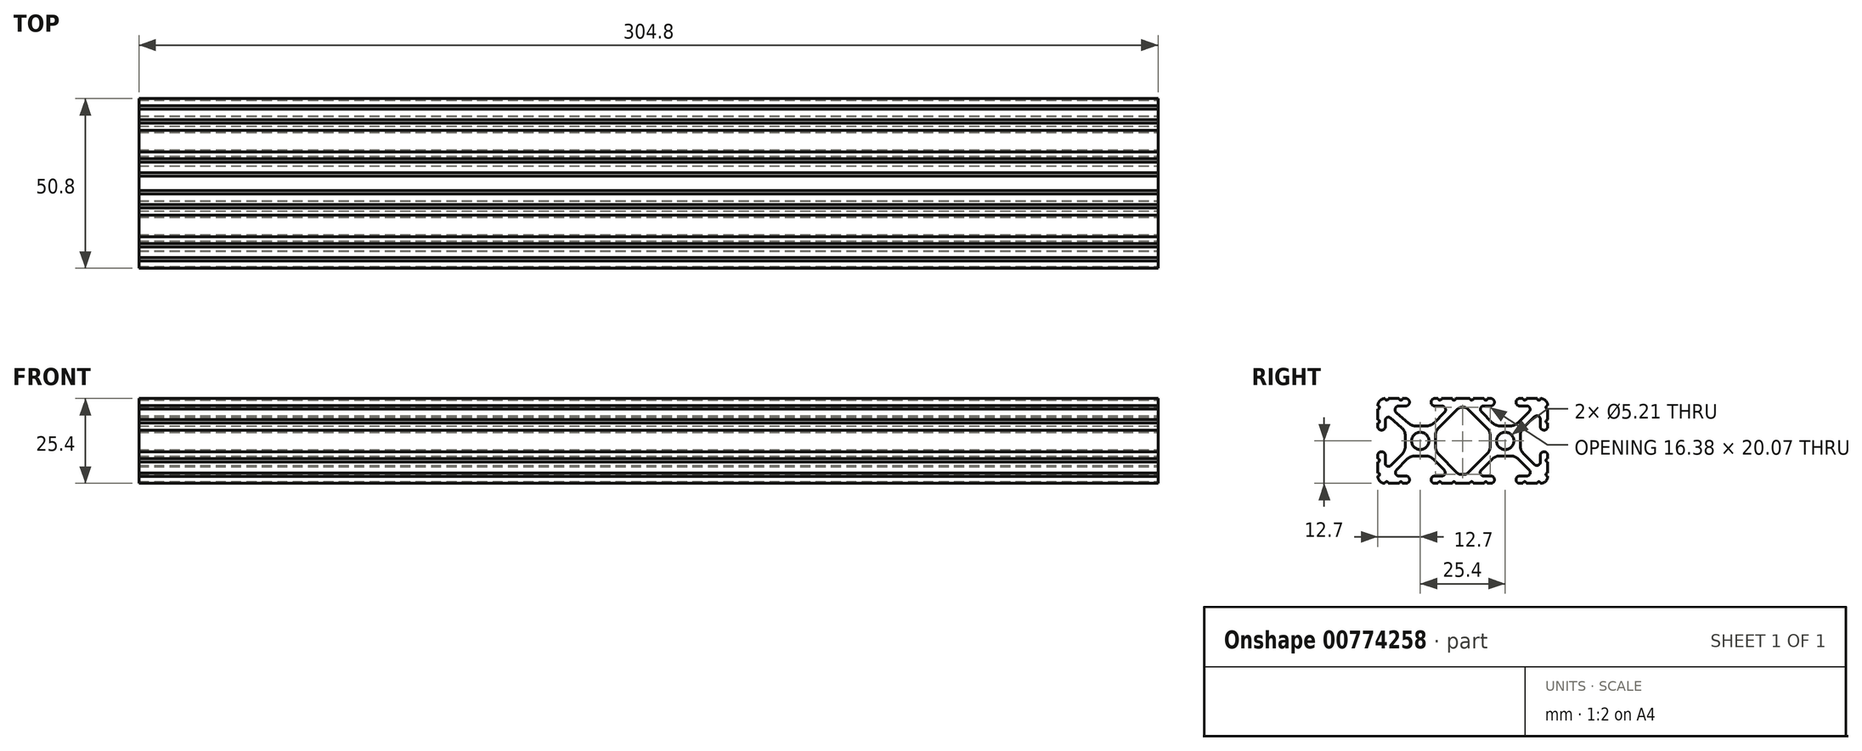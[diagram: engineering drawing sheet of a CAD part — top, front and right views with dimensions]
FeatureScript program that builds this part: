
annotation { "Feature Type Name" : "Feature", "Feature Type Description" : "" }
export const myFeature = defineFeature(function(context is Context, id is Id, definition is map)
    precondition{}
    {
        {
            var Q0;
            Q0=qCreatedBy(makeId("Right.planeOp"),FACE);
            var sketch = newSketch(context, id + "F0", { "sketchPlane" : qUnion([Q0])});
            skLineSegment(sketch, "E0", {"start": v(7.26, 3.87) * mm, "end": v(1.55, 9.57) * mm});
            skArc(sketch, "E1", {"start": v(1.55, 9.57) * mm, "mid": v(1.04, 9.91) * mm, "end": v(0.43, 10.03) * mm});
            skLineSegment(sketch, "E2", {"start": v(0.43, 10.03) * mm, "end": v(-0.43, 10.03) * mm});
            skArc(sketch, "E3", {"start": v(-0.43, 10.03) * mm, "mid": v(-1.04, 9.91) * mm, "end": v(-1.55, 9.57) * mm});
            skLineSegment(sketch, "E4", {"start": v(-1.55, 9.57) * mm, "end": v(-7.26, 3.87) * mm});
            skArc(sketch, "E5", {"start": v(-7.26, 3.87) * mm, "mid": v(-7.95, 2.84) * mm, "end": v(-8.2, 1.62) * mm});
            skLineSegment(sketch, "E6", {"start": v(-8.2, 1.62) * mm, "end": v(-8.2, -1.62) * mm});
            skLineSegment(sketch, "E7", {"start": v(-7.28, -3.85) * mm, "end": v(-1.68, -9.56) * mm});
            skArc(sketch, "E8", {"start": v(-1.68, -9.56) * mm, "mid": v(-1.16, -9.91) * mm, "end": v(-0.55, -10.03) * mm});
            skLineSegment(sketch, "E9", {"start": v(-0.55, -10.03) * mm, "end": v(0.4, -10.03) * mm});
            skArc(sketch, "E10", {"start": v(0.4, -10.03) * mm, "mid": v(1, -9.91) * mm, "end": v(1.5, -9.58) * mm});
            skLineSegment(sketch, "E11", {"start": v(1.5, -9.58) * mm, "end": v(7.25, -3.88) * mm});
            skArc(sketch, "E12", {"start": v(7.25, -3.88) * mm, "mid": v(7.95, -2.84) * mm, "end": v(8.2, -1.62) * mm});
            skLineSegment(sketch, "E13", {"start": v(8.2, -1.62) * mm, "end": v(8.2, 1.62) * mm});
            skArc(sketch, "E14", {"start": v(8.2, 1.62) * mm, "mid": v(7.95, 2.84) * mm, "end": v(7.26, 3.87) * mm});
            skCircle(sketch, "E15", {"center": v(12.7, 0) * mm, "radius": 2.6 * mm});
            skCircle(sketch, "E16", {"center": v(-12.7, 0) * mm, "radius": 2.6 * mm});
            skArc(sketch, "E17", {"start": v(-8.2, -1.62) * mm, "mid": v(-7.96, -2.82) * mm, "end": v(-7.28, -3.85) * mm});
            skLineSegment(sketch, "E18", {"start": v(-15.94, -11.65) * mm, "end": v(-15.94, -11.54) * mm});
            skArc(sketch, "E19", {"start": v(-15.94, -11.54) * mm, "mid": v(-16.25, -10.8) * mm, "end": v(-16.99, -10.5) * mm});
            skLineSegment(sketch, "E20", {"start": v(-16.99, -10.5) * mm, "end": v(-19.12, -10.5) * mm});
            skArc(sketch, "E21", {"start": v(-19.84, -8.77) * mm, "mid": v(-20.05, -9.87) * mm, "end": v(-19.12, -10.5) * mm});
            skLineSegment(sketch, "E22", {"start": v(-19.84, -8.77) * mm, "end": v(-16.62, -5.46) * mm});
            skArc(sketch, "E23", {"start": v(-14.34, -4.5) * mm, "mid": v(-15.58, -4.75) * mm, "end": v(-16.62, -5.46) * mm});
            skLineSegment(sketch, "E24", {"start": v(-14.34, -4.5) * mm, "end": v(-11.08, -4.5) * mm});
            skArc(sketch, "E25", {"start": v(-8.82, -5.45) * mm, "mid": v(-9.85, -4.74) * mm, "end": v(-11.08, -4.5) * mm});
            skLineSegment(sketch, "E26", {"start": v(-8.82, -5.45) * mm, "end": v(-5.56, -8.76) * mm});
            skArc(sketch, "E27", {"start": v(-6.29, -10.5) * mm, "mid": v(-5.35, -9.87) * mm, "end": v(-5.56, -8.76) * mm});
            skLineSegment(sketch, "E28", {"start": v(-6.29, -10.5) * mm, "end": v(-8.41, -10.5) * mm});
            skArc(sketch, "E29", {"start": v(-8.41, -10.5) * mm, "mid": v(-9.15, -10.8) * mm, "end": v(-9.46, -11.54) * mm});
            skLineSegment(sketch, "E30", {"start": v(-9.46, -11.54) * mm, "end": v(-9.46, -11.65) * mm});
            skArc(sketch, "E31", {"start": v(-9.46, -11.65) * mm, "mid": v(-9.15, -12.4) * mm, "end": v(-8.41, -12.7) * mm});
            skLineSegment(sketch, "E32", {"start": v(-8.41, -12.7) * mm, "end": v(-7.38, -12.7) * mm});
            skArc(sketch, "E33", {"start": v(-6.37, -12.7) * mm, "mid": v(-6.87, -12.2) * mm, "end": v(-7.38, -12.7) * mm});
            skLineSegment(sketch, "E34", {"start": v(-6.37, -12.7) * mm, "end": v(-3.15, -12.7) * mm});
            skArc(sketch, "E35", {"start": v(-2.13, -12.7) * mm, "mid": v(-2.64, -12.2) * mm, "end": v(-3.15, -12.7) * mm});
            skLineSegment(sketch, "E36", {"start": v(-2.13, -12.7) * mm, "end": v(2.13, -12.7) * mm});
            skArc(sketch, "E37", {"start": v(3.15, -12.7) * mm, "mid": v(2.64, -12.2) * mm, "end": v(2.13, -12.7) * mm});
            skLineSegment(sketch, "E38", {"start": v(3.15, -12.7) * mm, "end": v(6.37, -12.7) * mm});
            skArc(sketch, "E39", {"start": v(7.38, -12.7) * mm, "mid": v(6.87, -12.2) * mm, "end": v(6.37, -12.7) * mm});
            skLineSegment(sketch, "E40", {"start": v(7.38, -12.7) * mm, "end": v(8.41, -12.7) * mm});
            skArc(sketch, "E41", {"start": v(8.41, -12.7) * mm, "mid": v(9.15, -12.4) * mm, "end": v(9.46, -11.65) * mm});
            skLineSegment(sketch, "E42", {"start": v(9.46, -11.65) * mm, "end": v(9.46, -11.54) * mm});
            skArc(sketch, "E43", {"start": v(9.46, -11.54) * mm, "mid": v(9.15, -10.8) * mm, "end": v(8.41, -10.5) * mm});
            skLineSegment(sketch, "E44", {"start": v(8.41, -10.5) * mm, "end": v(6.28, -10.5) * mm});
            skArc(sketch, "E45", {"start": v(5.53, -8.67) * mm, "mid": v(5.3, -9.83) * mm, "end": v(6.28, -10.5) * mm});
            skLineSegment(sketch, "E46", {"start": v(5.53, -8.67) * mm, "end": v(8.8, -5.42) * mm});
            skArc(sketch, "E47", {"start": v(11.05, -4.5) * mm, "mid": v(9.84, -4.73) * mm, "end": v(8.8, -5.42) * mm});
            skLineSegment(sketch, "E48", {"start": v(11.05, -4.5) * mm, "end": v(14.35, -4.5) * mm});
            skArc(sketch, "E49", {"start": v(16.6, -5.42) * mm, "mid": v(15.56, -4.73) * mm, "end": v(14.35, -4.5) * mm});
            skLineSegment(sketch, "E50", {"start": v(16.6, -5.42) * mm, "end": v(19.87, -8.67) * mm});
            skArc(sketch, "E51", {"start": v(19.12, -10.5) * mm, "mid": v(20.1, -9.83) * mm, "end": v(19.87, -8.67) * mm});
            skLineSegment(sketch, "E52", {"start": v(19.12, -10.5) * mm, "end": v(16.99, -10.5) * mm});
            skArc(sketch, "E53", {"start": v(16.99, -10.5) * mm, "mid": v(16.25, -10.8) * mm, "end": v(15.94, -11.54) * mm});
            skLineSegment(sketch, "E54", {"start": v(15.94, -11.54) * mm, "end": v(15.94, -11.65) * mm});
            skArc(sketch, "E55", {"start": v(15.94, -11.65) * mm, "mid": v(16.25, -12.4) * mm, "end": v(16.99, -12.7) * mm});
            skLineSegment(sketch, "E56", {"start": v(16.99, -12.7) * mm, "end": v(18.02, -12.7) * mm});
            skArc(sketch, "E57", {"start": v(19.03, -12.7) * mm, "mid": v(18.53, -12.2) * mm, "end": v(18.02, -12.7) * mm});
            skLineSegment(sketch, "E58", {"start": v(19.03, -12.7) * mm, "end": v(22.25, -12.7) * mm});
            skArc(sketch, "E59", {"start": v(23.27, -12.7) * mm, "mid": v(22.76, -12.2) * mm, "end": v(22.25, -12.7) * mm});
            skArc(sketch, "E60", {"start": v(23.27, -12.7) * mm, "mid": v(24.78, -12.08) * mm, "end": v(25.4, -10.57) * mm});
            skArc(sketch, "E61", {"start": v(25.4, -9.55) * mm, "mid": v(24.9, -10.06) * mm, "end": v(25.4, -10.57) * mm});
            skLineSegment(sketch, "E62", {"start": v(25.4, -9.55) * mm, "end": v(25.4, -6.33) * mm});
            skArc(sketch, "E63", {"start": v(25.4, -5.32) * mm, "mid": v(24.9, -5.83) * mm, "end": v(25.4, -6.33) * mm});
            skLineSegment(sketch, "E64", {"start": v(25.4, -5.32) * mm, "end": v(25.4, -4.24) * mm});
            skArc(sketch, "E65", {"start": v(25.4, -4.24) * mm, "mid": v(25.1, -3.53) * mm, "end": v(24.4, -3.24) * mm});
            skLineSegment(sketch, "E66", {"start": v(24.4, -3.24) * mm, "end": v(24.24, -3.24) * mm});
            skArc(sketch, "E67", {"start": v(24.24, -3.24) * mm, "mid": v(23.5, -3.55) * mm, "end": v(23.2, -4.29) * mm});
            skLineSegment(sketch, "E68", {"start": v(23.2, -4.29) * mm, "end": v(23.2, -6.33) * mm});
            skArc(sketch, "E69", {"start": v(21.43, -7.07) * mm, "mid": v(22.56, -7.29) * mm, "end": v(23.2, -6.33) * mm});
            skLineSegment(sketch, "E70", {"start": v(21.43, -7.07) * mm, "end": v(18.15, -3.8) * mm});
            skArc(sketch, "E71", {"start": v(17.2, -1.55) * mm, "mid": v(17.45, -2.77) * mm, "end": v(18.15, -3.8) * mm});
            skLineSegment(sketch, "E72", {"start": v(17.2, -1.55) * mm, "end": v(17.2, 1.7) * mm});
            skArc(sketch, "E73", {"start": v(18.14, 3.94) * mm, "mid": v(17.45, 2.91) * mm, "end": v(17.2, 1.7) * mm});
            skLineSegment(sketch, "E74", {"start": v(18.14, 3.94) * mm, "end": v(21.43, 7.23) * mm});
            skArc(sketch, "E75", {"start": v(23.2, 6.5) * mm, "mid": v(22.55, 7.45) * mm, "end": v(21.43, 7.23) * mm});
            skLineSegment(sketch, "E76", {"start": v(23.2, 6.5) * mm, "end": v(23.2, 4.29) * mm});
            skArc(sketch, "E77", {"start": v(23.2, 4.29) * mm, "mid": v(23.5, 3.55) * mm, "end": v(24.24, 3.24) * mm});
            skLineSegment(sketch, "E78", {"start": v(24.24, 3.24) * mm, "end": v(24.35, 3.24) * mm});
            skArc(sketch, "E79", {"start": v(24.35, 3.24) * mm, "mid": v(25.1, 3.55) * mm, "end": v(25.4, 4.29) * mm});
            skLineSegment(sketch, "E80", {"start": v(25.4, 4.29) * mm, "end": v(25.4, 5.32) * mm});
            skArc(sketch, "E81", {"start": v(25.4, 6.33) * mm, "mid": v(24.9, 5.83) * mm, "end": v(25.4, 5.32) * mm});
            skLineSegment(sketch, "E82", {"start": v(25.4, 6.33) * mm, "end": v(25.4, 9.55) * mm});
            skArc(sketch, "E83", {"start": v(25.4, 10.57) * mm, "mid": v(24.9, 10.06) * mm, "end": v(25.4, 9.55) * mm});
            skArc(sketch, "E84", {"start": v(25.4, 10.57) * mm, "mid": v(24.78, 12.08) * mm, "end": v(23.27, 12.7) * mm});
            skArc(sketch, "E85", {"start": v(22.25, 12.7) * mm, "mid": v(22.76, 12.2) * mm, "end": v(23.27, 12.7) * mm});
            skLineSegment(sketch, "E86", {"start": v(22.25, 12.7) * mm, "end": v(19.03, 12.7) * mm});
            skArc(sketch, "E87", {"start": v(18.02, 12.7) * mm, "mid": v(18.53, 12.2) * mm, "end": v(19.03, 12.7) * mm});
            skLineSegment(sketch, "E88", {"start": v(18.02, 12.7) * mm, "end": v(16.99, 12.7) * mm});
            skArc(sketch, "E89", {"start": v(16.99, 12.7) * mm, "mid": v(16.25, 12.4) * mm, "end": v(15.94, 11.65) * mm});
            skLineSegment(sketch, "E90", {"start": v(15.94, 11.65) * mm, "end": v(15.94, 11.54) * mm});
            skArc(sketch, "E91", {"start": v(15.94, 11.54) * mm, "mid": v(16.25, 10.8) * mm, "end": v(16.99, 10.5) * mm});
            skLineSegment(sketch, "E92", {"start": v(16.99, 10.5) * mm, "end": v(19.12, 10.5) * mm});
            skArc(sketch, "E93", {"start": v(19.83, 8.76) * mm, "mid": v(20.06, 9.86) * mm, "end": v(19.12, 10.5) * mm});
            skLineSegment(sketch, "E94", {"start": v(19.83, 8.76) * mm, "end": v(16.5, 5.42) * mm});
            skArc(sketch, "E95", {"start": v(14.25, 4.5) * mm, "mid": v(15.47, 4.74) * mm, "end": v(16.5, 5.42) * mm});
            skLineSegment(sketch, "E96", {"start": v(14.25, 4.5) * mm, "end": v(11.15, 4.5) * mm});
            skArc(sketch, "E97", {"start": v(8.9, 5.42) * mm, "mid": v(9.93, 4.74) * mm, "end": v(11.15, 4.5) * mm});
            skLineSegment(sketch, "E98", {"start": v(8.9, 5.42) * mm, "end": v(5.57, 8.76) * mm});
            skArc(sketch, "E99", {"start": v(6.28, 10.5) * mm, "mid": v(5.34, 9.86) * mm, "end": v(5.57, 8.76) * mm});
            skLineSegment(sketch, "E100", {"start": v(6.28, 10.5) * mm, "end": v(8.41, 10.5) * mm});
            skArc(sketch, "E101", {"start": v(8.41, 10.5) * mm, "mid": v(9.15, 10.8) * mm, "end": v(9.46, 11.54) * mm});
            skLineSegment(sketch, "E102", {"start": v(9.46, 11.54) * mm, "end": v(9.46, 11.65) * mm});
            skArc(sketch, "E103", {"start": v(9.46, 11.65) * mm, "mid": v(9.15, 12.4) * mm, "end": v(8.41, 12.7) * mm});
            skLineSegment(sketch, "E104", {"start": v(8.41, 12.7) * mm, "end": v(7.38, 12.7) * mm});
            skArc(sketch, "E105", {"start": v(6.37, 12.7) * mm, "mid": v(6.87, 12.2) * mm, "end": v(7.38, 12.7) * mm});
            skLineSegment(sketch, "E106", {"start": v(6.37, 12.7) * mm, "end": v(3.15, 12.7) * mm});
            skArc(sketch, "E107", {"start": v(2.13, 12.7) * mm, "mid": v(2.64, 12.2) * mm, "end": v(3.15, 12.7) * mm});
            skLineSegment(sketch, "E108", {"start": v(2.13, 12.7) * mm, "end": v(-2.13, 12.7) * mm});
            skArc(sketch, "E109", {"start": v(-3.15, 12.7) * mm, "mid": v(-2.64, 12.2) * mm, "end": v(-2.13, 12.7) * mm});
            skLineSegment(sketch, "E110", {"start": v(-3.15, 12.7) * mm, "end": v(-6.37, 12.7) * mm});
            skArc(sketch, "E111", {"start": v(-7.38, 12.7) * mm, "mid": v(-6.87, 12.2) * mm, "end": v(-6.37, 12.7) * mm});
            skLineSegment(sketch, "E112", {"start": v(-7.38, 12.7) * mm, "end": v(-8.41, 12.7) * mm});
            skArc(sketch, "E113", {"start": v(-8.41, 12.7) * mm, "mid": v(-9.15, 12.4) * mm, "end": v(-9.46, 11.65) * mm});
            skLineSegment(sketch, "E114", {"start": v(-9.46, 11.65) * mm, "end": v(-9.46, 11.54) * mm});
            skArc(sketch, "E115", {"start": v(-9.46, 11.54) * mm, "mid": v(-9.15, 10.8) * mm, "end": v(-8.41, 10.5) * mm});
            skLineSegment(sketch, "E116", {"start": v(-8.41, 10.5) * mm, "end": v(-6.29, 10.5) * mm});
            skArc(sketch, "E117", {"start": v(-5.48, 8.54) * mm, "mid": v(-5.23, 9.78) * mm, "end": v(-6.29, 10.5) * mm});
            skLineSegment(sketch, "E118", {"start": v(-5.48, 8.54) * mm, "end": v(-8.6, 5.42) * mm});
            skArc(sketch, "E119", {"start": v(-10.84, 4.5) * mm, "mid": v(-9.63, 4.74) * mm, "end": v(-8.6, 5.42) * mm});
            skLineSegment(sketch, "E120", {"start": v(-10.84, 4.5) * mm, "end": v(-14.1, 4.5) * mm});
            skArc(sketch, "E121", {"start": v(-16.19, 5.28) * mm, "mid": v(-15.22, 4.7) * mm, "end": v(-14.1, 4.5) * mm});
            skLineSegment(sketch, "E122", {"start": v(-16.19, 5.28) * mm, "end": v(-19.87, 8.48) * mm});
            skArc(sketch, "E123", {"start": v(-19.12, 10.5) * mm, "mid": v(-20.19, 9.75) * mm, "end": v(-19.87, 8.48) * mm});
            skLineSegment(sketch, "E124", {"start": v(-19.12, 10.5) * mm, "end": v(-16.99, 10.5) * mm});
            skArc(sketch, "E125", {"start": v(-16.99, 10.5) * mm, "mid": v(-16.25, 10.8) * mm, "end": v(-15.94, 11.54) * mm});
            skLineSegment(sketch, "E126", {"start": v(-15.94, 11.54) * mm, "end": v(-15.94, 11.65) * mm});
            skArc(sketch, "E127", {"start": v(-15.94, 11.65) * mm, "mid": v(-16.25, 12.4) * mm, "end": v(-16.99, 12.7) * mm});
            skLineSegment(sketch, "E128", {"start": v(-16.99, 12.7) * mm, "end": v(-18.02, 12.7) * mm});
            skArc(sketch, "E129", {"start": v(-19.03, 12.7) * mm, "mid": v(-18.53, 12.2) * mm, "end": v(-18.02, 12.7) * mm});
            skLineSegment(sketch, "E130", {"start": v(-19.03, 12.7) * mm, "end": v(-22.25, 12.7) * mm});
            skArc(sketch, "E131", {"start": v(-23.27, 12.7) * mm, "mid": v(-22.76, 12.2) * mm, "end": v(-22.25, 12.7) * mm});
            skArc(sketch, "E132", {"start": v(-23.27, 12.7) * mm, "mid": v(-24.78, 12.08) * mm, "end": v(-25.4, 10.57) * mm});
            skArc(sketch, "E133", {"start": v(-25.4, 9.55) * mm, "mid": v(-24.9, 10.06) * mm, "end": v(-25.4, 10.57) * mm});
            skLineSegment(sketch, "E134", {"start": v(-25.4, 9.55) * mm, "end": v(-25.4, 6.33) * mm});
            skArc(sketch, "E135", {"start": v(-25.4, 5.32) * mm, "mid": v(-24.9, 5.83) * mm, "end": v(-25.4, 6.33) * mm});
            skLineSegment(sketch, "E136", {"start": v(-25.4, 5.32) * mm, "end": v(-25.4, 4.24) * mm});
            skArc(sketch, "E137", {"start": v(-25.4, 4.24) * mm, "mid": v(-25.1, 3.53) * mm, "end": v(-24.4, 3.24) * mm});
            skLineSegment(sketch, "E138", {"start": v(-24.4, 3.24) * mm, "end": v(-24.19, 3.24) * mm});
            skArc(sketch, "E139", {"start": v(-24.19, 3.24) * mm, "mid": v(-23.48, 3.53) * mm, "end": v(-23.2, 4.24) * mm});
            skLineSegment(sketch, "E140", {"start": v(-23.2, 4.24) * mm, "end": v(-23.2, 6.16) * mm});
            skArc(sketch, "E141", {"start": v(-21.58, 6.89) * mm, "mid": v(-22.62, 7.04) * mm, "end": v(-23.2, 6.16) * mm});
            skLineSegment(sketch, "E142", {"start": v(-21.58, 6.89) * mm, "end": v(-18.3, 4.02) * mm});
            skArc(sketch, "E143", {"start": v(-17.2, 1.63) * mm, "mid": v(-17.5, 2.95) * mm, "end": v(-18.3, 4.02) * mm});
            skLineSegment(sketch, "E144", {"start": v(-17.2, 1.63) * mm, "end": v(-17.2, -1.63) * mm});
            skArc(sketch, "E145", {"start": v(-18.1, -3.85) * mm, "mid": v(-17.44, -2.83) * mm, "end": v(-17.2, -1.63) * mm});
            skLineSegment(sketch, "E146", {"start": v(-18.1, -3.85) * mm, "end": v(-21.53, -7.35) * mm});
            skArc(sketch, "E147", {"start": v(-23.2, -6.68) * mm, "mid": v(-22.59, -7.57) * mm, "end": v(-21.53, -7.35) * mm});
            skLineSegment(sketch, "E148", {"start": v(-23.2, -6.68) * mm, "end": v(-23.2, -4.24) * mm});
            skArc(sketch, "E149", {"start": v(-23.2, -4.24) * mm, "mid": v(-23.48, -3.53) * mm, "end": v(-24.19, -3.24) * mm});
            skLineSegment(sketch, "E150", {"start": v(-24.19, -3.24) * mm, "end": v(-24.4, -3.24) * mm});
            skArc(sketch, "E151", {"start": v(-24.4, -3.24) * mm, "mid": v(-25.1, -3.53) * mm, "end": v(-25.4, -4.24) * mm});
            skLineSegment(sketch, "E152", {"start": v(-25.4, -4.24) * mm, "end": v(-25.4, -5.32) * mm});
            skArc(sketch, "E153", {"start": v(-25.4, -6.33) * mm, "mid": v(-24.9, -5.83) * mm, "end": v(-25.4, -5.32) * mm});
            skLineSegment(sketch, "E154", {"start": v(-25.4, -6.33) * mm, "end": v(-25.4, -9.55) * mm});
            skArc(sketch, "E155", {"start": v(-25.4, -10.57) * mm, "mid": v(-24.9, -10.06) * mm, "end": v(-25.4, -9.55) * mm});
            skArc(sketch, "E156", {"start": v(-25.4, -10.57) * mm, "mid": v(-24.78, -12.08) * mm, "end": v(-23.27, -12.7) * mm});
            skArc(sketch, "E157", {"start": v(-22.25, -12.7) * mm, "mid": v(-22.76, -12.2) * mm, "end": v(-23.27, -12.7) * mm});
            skLineSegment(sketch, "E158", {"start": v(-22.25, -12.7) * mm, "end": v(-19.03, -12.7) * mm});
            skArc(sketch, "E159", {"start": v(-18.02, -12.7) * mm, "mid": v(-18.53, -12.2) * mm, "end": v(-19.03, -12.7) * mm});
            skLineSegment(sketch, "E160", {"start": v(-18.02, -12.7) * mm, "end": v(-16.99, -12.7) * mm});
            skArc(sketch, "E161", {"start": v(-16.99, -12.7) * mm, "mid": v(-16.25, -12.4) * mm, "end": v(-15.94, -11.65) * mm});
            skSolve(sketch);
        }
        {
            var Q0;
            Q0 = qSketchRegion(id + "F0", true);
            extrude(context, id + "F1", {"entities" : qUnion([Q0]), "oppositeDirection" : true, "depth" : 304.8 * mm, "offsetDistance" : 25.4 * mm});
        }
    });
